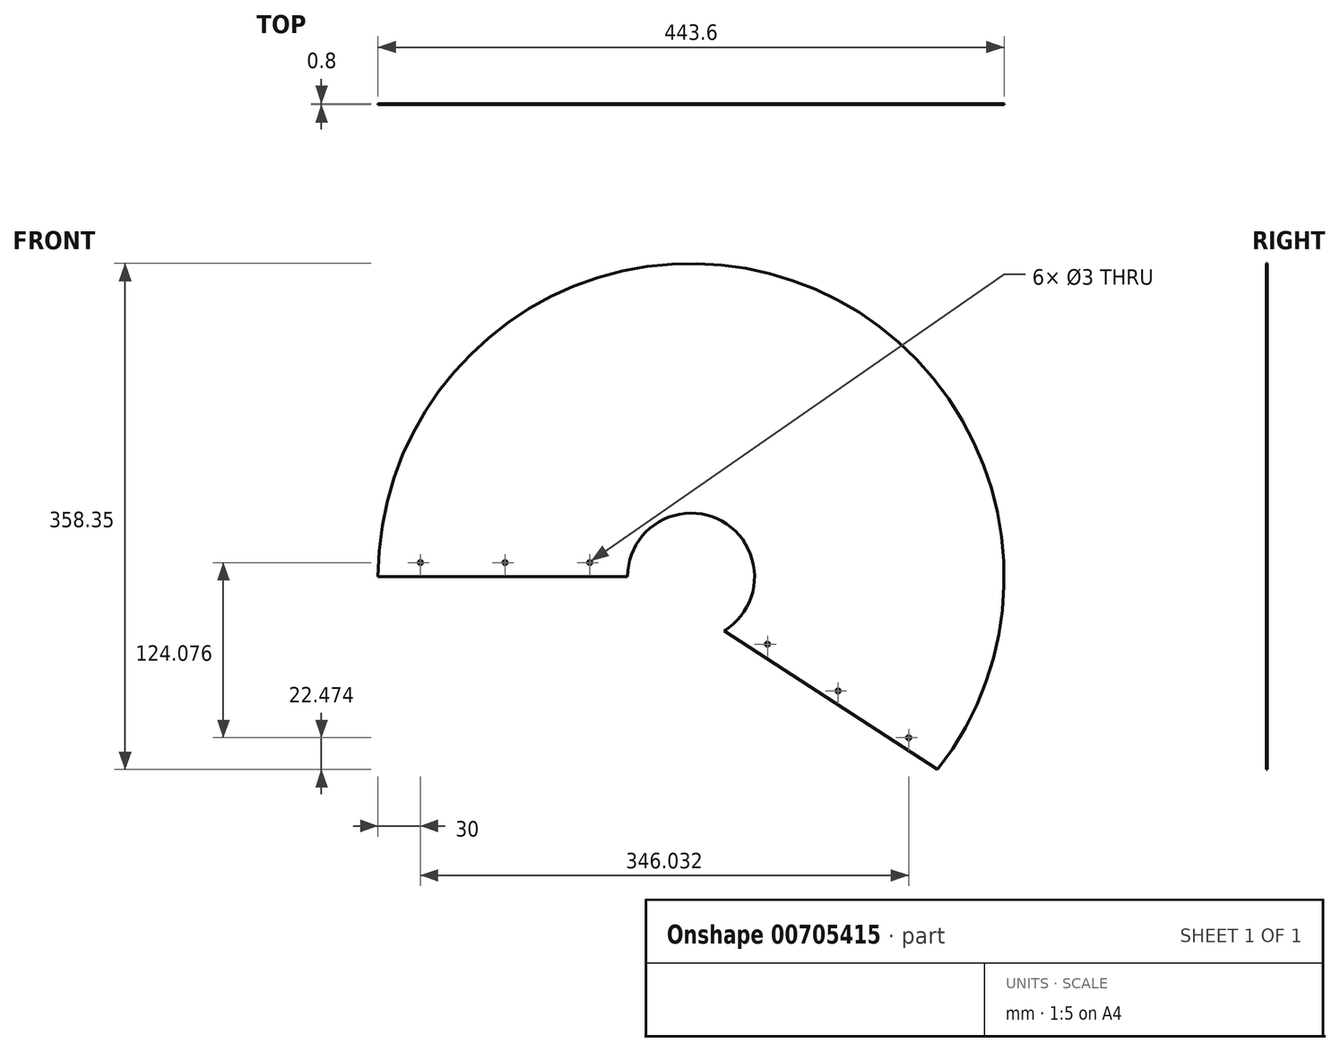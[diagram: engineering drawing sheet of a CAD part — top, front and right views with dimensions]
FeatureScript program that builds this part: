
annotation { "Feature Type Name" : "Feature", "Feature Type Description" : "" }
export const myFeature = defineFeature(function(context is Context, id is Id, definition is map)
    precondition{}
    {
        {
            var Q0;
            Q0=qCreatedBy(makeId("Front.planeOp"),FACE);
            var sketch = newSketch(context, id + "F0", { "sketchPlane" : qUnion([Q0])});
            skCircle(sketch, "E0", {"center": v(0, 0) * mm, "radius": 45 * mm, "construction": true});
            skCircle(sketch, "E1", {"center": v(0, 0) * mm, "radius": 221.8 * mm, "construction": true});
            skSolve(sketch);
        }
        {
            var Q0;
            Q0=qCreatedBy(makeId("Front.planeOp"),FACE);
            var sketch = newSketch(context, id + "F1", { "sketchPlane" : qUnion([Q0])});
            skLineSegment(sketch, "E2", {"start": v(0, 0) * mm, "end": v(-221.8, 0) * mm, "construction": true});
            skLineSegment(sketch, "E3", {"start": v(0, 0) * mm, "end": v(174.78, -136.55) * mm, "construction": true});
            skLineSegment(sketch, "E4", {"start": v(0, 0) * mm, "end": v(115.43, -189.4) * mm, "construction": true});
            skLineSegment(sketch, "E5", {"start": v(0, 0) * mm, "end": v(184.96, -122.42) * mm, "construction": true});
            skSolve(sketch);
        }
        {
            var Q0;
            Q0=qCreatedBy(makeId("Front.planeOp"),FACE);
            var sketch = newSketch(context, id + "F2", { "sketchPlane" : qUnion([Q0])});
            skArc(sketch, "E6", {"start": v(23.42, -38.43) * mm, "mid": v(22.04, 39.24) * mm, "end": v(-45, 0) * mm});
            skArc(sketch, "E7", {"start": v(174.78, -136.55) * mm, "mid": v(72.21, 209.72) * mm, "end": v(-221.8, 0) * mm});
            skLineSegment(sketch, "E8", {"start": v(-45, 0) * mm, "end": v(-221.8, 0) * mm});
            skLineSegment(sketch, "E9", {"start": v(23.42, -38.43) * mm, "end": v(174.78, -136.55) * mm});
            skSolve(sketch);
        }
        {
            var Q0;
            Q0 = qSketchRegion(id + "F2", true);
            extrude(context, id + "F3", {"entities" : qUnion([Q0]), "depth" : 0.8 * mm, "offsetDistance" : 25 * mm});
        }
        {
            var Q0;
            Q0=makeQuery(id+"F3.opExtrude","CAP_FACE",FACE,{"disambiguationData":[OSD([sQuery(id+"F2.wireOp",EDGE,"E6"),sQuery(id+"F2.wireOp",EDGE,"E7"),sQuery(id+"F2.wireOp",EDGE,"E8"),sQuery(id+"F2.wireOp",EDGE,"E9")])],"isStart":false});
            var sketch = newSketch(context, id + "F4", { "sketchPlane" : qUnion([Q0])});
            skCircle(sketch, "E10", {"center": v(-191.8, 10) * mm, "radius": 1.5 * mm});
            skLineSegment(sketch, "E11", {"start": v(-43.87, 10) * mm, "end": v(-221.57, 10) * mm, "construction": true});
            skCircle(sketch, "E12", {"center": v(-131.8, 10) * mm, "radius": 1.5 * mm});
            skCircle(sketch, "E13", {"center": v(-71.8, 10) * mm, "radius": 1.5 * mm});
            skLineSegment(sketch, "E14", {"start": v(31.07, -32.55) * mm, "end": v(179.25, -130.63) * mm, "construction": true});
            skCircle(sketch, "E15", {"center": v(154.23, -114.08) * mm, "radius": 1.5 * mm});
            skCircle(sketch, "E16", {"center": v(104.2, -80.96) * mm, "radius": 1.5 * mm});
            skCircle(sketch, "E17", {"center": v(54.17, -47.84) * mm, "radius": 1.5 * mm});
            skSolve(sketch);
        }
        {
            var Q0;
            Q0 = qSketchRegion(id + "F4", true);
            extrude(context, id + "F5", {"entities" : qUnion([Q0]), "operationType" : NewBodyOperationType.REMOVE, "oppositeDirection" : true, "depth" : 25 * mm, "offsetDistance" : 25 * mm});
        }
    });
